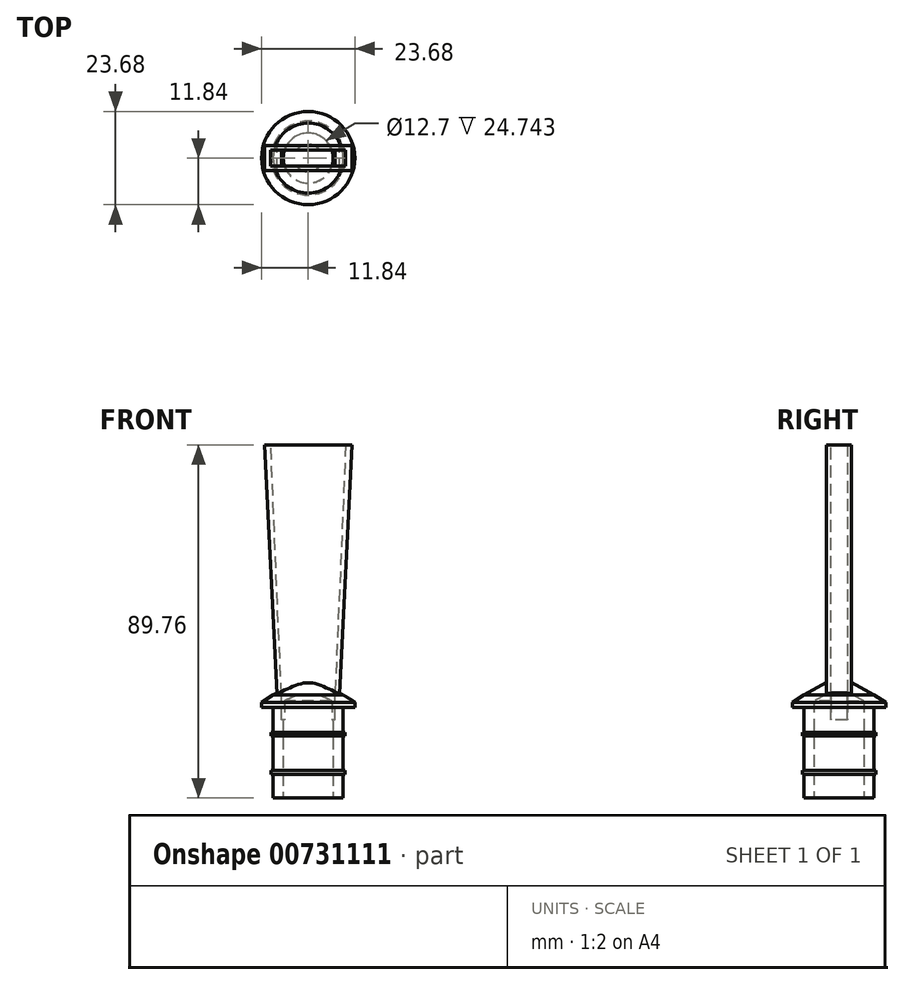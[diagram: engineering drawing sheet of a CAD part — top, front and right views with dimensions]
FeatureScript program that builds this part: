
annotation { "Feature Type Name" : "Feature", "Feature Type Description" : "" }
export const myFeature = defineFeature(function(context is Context, id is Id, definition is map)
    precondition{}
    {
        {
            var Q0;
            Q0=qCreatedBy(makeId("Top.planeOp"),FACE);
            var sketch = newSketch(context, id + "F0", { "sketchPlane" : qUnion([Q0])});
            skCircle(sketch, "E0", {"center": v(0, 0) * mm, "radius": 8.9 * mm});
            skSolve(sketch);
        }
        {
            var Q0;
            Q0=qSketchRegion(id+"F0",true);
            extrude(context, id + "F1", {"entities" : qUnion([Q0]), "depth" : 6.05 * mm, "offsetDistance" : 25.4 * mm});
        }
        {
            var Q0;
            Q0=makeQuery(id+"F1.opExtrude","CAP_FACE",FACE,{"disambiguationData":[OSD([sQuery(id+"F0.wireOp",EDGE,"E0")])],"isStart":false});
            var sketch = newSketch(context, id + "F2", { "sketchPlane" : qUnion([Q0])});
            skCircle(sketch, "E1", {"center": v(0, 0) * mm, "radius": 9.39 * mm});
            skSolve(sketch);
        }
        {
            var Q0;
            Q0=qSketchRegion(id+"F2",true);
            extrude(context, id + "F3", {"entities" : qUnion([Q0]), "operationType" : NewBodyOperationType.ADD, "depth" : 0.94 * mm, "offsetDistance" : 25.4 * mm});
        }
        {
            var Q0;
            Q0=makeQuery(id+"F3.opExtrude","CAP_FACE",FACE,{"disambiguationData":[OSD([sQuery(id+"F2.wireOp",EDGE,"E1")])],"isStart":false});
            var sketch = newSketch(context, id + "F4", { "sketchPlane" : qUnion([Q0])});
            skCircle(sketch, "E2", {"center": v(0, 0) * mm, "radius": 8.9 * mm});
            skSolve(sketch);
        }
        {
            var Q0;
            Q0=makeQuery(id+"F4.imprint","IMPRINT",FACE,{"disambiguationData":[TD([[makeQuery(id+"F4.imprint","IMPRINT",EDGE,{"derivedFrom":sQuery(id+"F4.wireOp",EDGE,"E2")}),1.0]])]});
            extrude(context, id + "F5", {"entities" : qUnion([Q0]), "operationType" : NewBodyOperationType.ADD, "depth" : 8.76 * mm, "offsetDistance" : 25.4 * mm});
        }
        {
            var Q0;
            Q0=makeQuery(id+"F5.opExtrude","CAP_FACE",FACE,{"disambiguationData":[OSD([sQuery(id+"F4.wireOp",EDGE,"E2")])],"isStart":false});
            var sketch = newSketch(context, id + "F6", { "sketchPlane" : qUnion([Q0])});
            skCircle(sketch, "E3", {"center": v(0, 0) * mm, "radius": 9.39 * mm});
            skSolve(sketch);
        }
        {
            var Q0;
            Q0=qSketchRegion(id+"F6",true);
            extrude(context, id + "F7", {"entities" : qUnion([Q0]), "operationType" : NewBodyOperationType.ADD, "depth" : 1 * mm, "offsetDistance" : 25.4 * mm});
        }
        {
            var Q0;
            Q0=makeQuery(id+"F7.opExtrude","CAP_FACE",FACE,{"disambiguationData":[OSD([sQuery(id+"F6.wireOp",EDGE,"E3")])],"isStart":false});
            var sketch = newSketch(context, id + "F8", { "sketchPlane" : qUnion([Q0])});
            skCircle(sketch, "E4", {"center": v(0, 0) * mm, "radius": 8.9 * mm});
            skSolve(sketch);
        }
        {
            var Q0;
            Q0=qSketchRegion(id+"F8",true);
            extrude(context, id + "F9", {"entities" : qUnion([Q0]), "operationType" : NewBodyOperationType.ADD, "depth" : 6.35 * mm, "offsetDistance" : 25.4 * mm});
        }
        {
            var Q0;
            Q0=qCreatedBy(makeId("Right.planeOp"),FACE);
            var sketch = newSketch(context, id + "F10", { "sketchPlane" : qUnion([Q0])});
            skLineSegment(sketch, "E5", {"start": v(0, 23.09) * mm, "end": v(-11.84, 23.09) * mm});
            skLineSegment(sketch, "E6", {"start": v(-11.84, 23.09) * mm, "end": v(-11.84, 24.36) * mm});
            skLineSegment(sketch, "E7", {"start": v(-11.84, 24.36) * mm, "end": v(-8.9, 26.26) * mm});
            skLineSegment(sketch, "E8", {"start": v(-8.9, 26.26) * mm, "end": v(0, 26.26) * mm});
            skLineSegment(sketch, "E9", {"start": v(0, 26.26) * mm, "end": v(0, 23.09) * mm});
            skSolve(sketch);
        }
        {
            var Q0;
            Q0=makeQuery(id+"F10.imprint","IMPRINT",FACE,{"disambiguationData":[TD([[makeQuery(id+"F10.imprint","IMPRINT",EDGE,{"derivedFrom":sQuery(id+"F10.wireOp",EDGE,"E5")}),-1.0]])]});
            var Q1;
            Q1=makeQuery(id+"F9.opExtrude","SWEPT_FACE",FACE,{"disambiguationData":[OSD([sQuery(id+"F8.wireOp",EDGE,"E4")])]});
            revolve(context, id + "F11", {"operationType" : NewBodyOperationType.ADD, "surfaceOperationType" : NewSurfaceOperationType.NEW, "entities" : qUnion([Q0]), "axis" : qUnion([Q1]), "revolveType" : RevolveType.FULL});
        }
        {
            var Q0;
            Q0=makeQuery(id+"F11.opRevolve","SWEPT_FACE",FACE,{"disambiguationData":[OSD([sQuery(id+"F10.wireOp",EDGE,"E8")])]});
            var sketch = newSketch(context, id + "F12", { "sketchPlane" : qUnion([Q0])});
            skCircle(sketch, "E10", {"center": v(0, 0) * mm, "radius": 8.9 * mm});
            skSolve(sketch);
        }
        {
            var Q0;
            Q0=makeQuery(id+"F12.imprint","IMPRINT",FACE,{"disambiguationData":[TD([[makeQuery(id+"F12.imprint","IMPRINT",EDGE,{"derivedFrom":sQuery(id+"F12.wireOp",EDGE,"E10")}),1.0]])]});
            cPlane(context, id + "F13", {"entities" : qUnion([Q0]), "cplaneType" : CPlaneType.OFFSET, "offset" : 0 * mm, "width" : 152.4 * mm, "height" : 152.4 * mm});
        }
        {
            var Q0;
            Q0=qCreatedBy(id+"F13.planeOp",FACE);
            var sketch = newSketch(context, id + "F14", { "sketchPlane" : qUnion([Q0])});
            skLineSegment(sketch, "E11.bottom", {"start": v(-7.94, 3.17) * mm, "end": v(7.94, 3.17) * mm});
            skLineSegment(sketch, "E11.top", {"start": v(-7.94, -3.18) * mm, "end": v(7.94, -3.18) * mm});
            skLineSegment(sketch, "E11.left", {"start": v(-7.94, 3.17) * mm, "end": v(-7.94, -3.18) * mm});
            skLineSegment(sketch, "E11.right", {"start": v(7.94, 3.17) * mm, "end": v(7.94, -3.18) * mm});
            skLineSegment(sketch, "E12", {"start": v(-7.94, 3.18) * mm, "end": v(7.94, -3.18) * mm, "construction": true});
            skPoint(sketch, "E13", {"position": v(0, 0) * mm});
            skSolve(sketch);
        }
        {
            var Q0;
            Q0=qCreatedBy(makeId("Right.planeOp"),FACE);
            var sketch = newSketch(context, id + "F15", { "sketchPlane" : qUnion([Q0])});
            skLineSegment(sketch, "E14", {"start": v(0, 26.26) * mm, "end": v(8.9, 26.26) * mm});
            skLineSegment(sketch, "E15", {"start": v(8.9, 26.26) * mm, "end": v(0, 31.03) * mm});
            skLineSegment(sketch, "E16", {"start": v(0, 31.03) * mm, "end": v(0, 26.26) * mm});
            skLineSegment(sketch, "E17", {"start": v(8.9, 26.26) * mm, "end": v(11.84, 24.36) * mm, "construction": true});
            skSolve(sketch);
        }
        {
            var Q0;
            Q0=makeQuery(id+"F15.imprint","IMPRINT",FACE,{"disambiguationData":[TD([[makeQuery(id+"F15.imprint","IMPRINT",EDGE,{"derivedFrom":sQuery(id+"F15.wireOp",EDGE,"E14")}),1.0]])]});
            var Q1;
            Q1=makeQuery(id+"F5.opExtrude","SWEPT_FACE",FACE,{"disambiguationData":[OSD([sQuery(id+"F4.wireOp",EDGE,"E2")])]});
            revolve(context, id + "F16", {"operationType" : NewBodyOperationType.ADD, "surfaceOperationType" : NewSurfaceOperationType.NEW, "entities" : qUnion([Q0]), "axis" : qUnion([Q1]), "revolveType" : RevolveType.FULL});
        }
        {
            var Q0;
            Q0=qCreatedBy(id+"F13.planeOp",FACE);
            cPlane(context, id + "F17", {"entities" : qUnion([Q0]), "cplaneType" : CPlaneType.OFFSET, "offset" : 63.5 * mm, "width" : 152.4 * mm, "height" : 152.4 * mm});
        }
        {
            var Q0;
            Q0=qCreatedBy(id+"F17.planeOp",FACE);
            var sketch = newSketch(context, id + "F18", { "sketchPlane" : qUnion([Q0])});
            skLineSegment(sketch, "E18.bottom", {"start": v(-5.56, 3.18) * mm, "end": v(5.56, 3.18) * mm});
            skLineSegment(sketch, "E18.top", {"start": v(-5.56, -3.18) * mm, "end": v(5.56, -3.18) * mm});
            skLineSegment(sketch, "E18.left", {"start": v(-5.56, 3.18) * mm, "end": v(-5.56, -3.18) * mm});
            skLineSegment(sketch, "E18.right", {"start": v(5.56, 3.18) * mm, "end": v(5.56, -3.18) * mm});
            skLineSegment(sketch, "E19", {"start": v(-5.56, 3.18) * mm, "end": v(5.56, -3.18) * mm, "construction": true});
            skPoint(sketch, "E20", {"position": v(0, 0) * mm});
            skSolve(sketch);
        }
        {
            var Q1;
            Q1=qSketchRegion(id+"F14",true);
            var Q2;
            Q2=qSketchRegion(id+"F18",true);
            loft(context, id + "F19", {"operationType" : NewBodyOperationType.ADD, "sheetProfilesArray" : [{ "sheetProfileEntities" : qUnion([Q1]) }, { "sheetProfileEntities" : qUnion([Q2]) }]});
        }
        {
            var Q0;
            Q0=makeQuery(id+"F19.opLoft","CAP_FACE",FACE,{"disambiguationData":[OSD([makeQuery(id+"F18.imprint","IMPRINT",FACE,{"disambiguationData":[TD([[makeQuery(id+"F18.imprint","IMPRINT",EDGE,{"derivedFrom":sQuery(id+"F18.wireOp",EDGE,"E18.bottom")}),-1.0]])]})])],"isStart":true});
            var sketch = newSketch(context, id + "F20", { "sketchPlane" : qUnion([Q0])});
            skLineSegment(sketch, "E21.bottom", {"start": v(-4.44, 2.06) * mm, "end": v(4.45, 2.06) * mm});
            skLineSegment(sketch, "E21.top", {"start": v(-4.44, -2.06) * mm, "end": v(4.45, -2.06) * mm});
            skLineSegment(sketch, "E21.left", {"start": v(-4.45, 2.06) * mm, "end": v(-4.45, -2.06) * mm});
            skLineSegment(sketch, "E21.right", {"start": v(4.45, 2.06) * mm, "end": v(4.45, -2.06) * mm});
            skSolve(sketch);
        }
        {
            var Q0;
            Q0=qCreatedBy(id+"F13.planeOp",FACE);
            var sketch = newSketch(context, id + "F21", { "sketchPlane" : qUnion([Q0])});
            skLineSegment(sketch, "E22.bottom", {"start": v(-6.82, 2.06) * mm, "end": v(6.82, 2.06) * mm});
            skLineSegment(sketch, "E22.top", {"start": v(-6.82, -2.06) * mm, "end": v(6.82, -2.06) * mm});
            skLineSegment(sketch, "E22.left", {"start": v(-6.82, 2.06) * mm, "end": v(-6.82, -2.06) * mm});
            skLineSegment(sketch, "E22.right", {"start": v(6.82, 2.06) * mm, "end": v(6.82, -2.06) * mm});
            skFitSpline(sketch, "E23.0", {"points": [v(-7.93, -3.18) * mm, v(-7.92, -2.13) * mm, v(-7.92, -0.8) * mm, v(-7.92, 0.79) * mm, v(-7.92, 1.86) * mm, v(-7.93, 2.65) * mm, v(-7.93, 3.17) * mm], "construction": true});
            skFitSpline(sketch, "E24.0", {"points": [v(7.93, 3.18) * mm, v(7.92, 2.13) * mm, v(7.92, 0.8) * mm, v(7.92, -0.79) * mm, v(7.92, -1.86) * mm, v(7.93, -2.65) * mm, v(7.93, -3.18) * mm], "construction": true});
            skSolve(sketch);
        }
        {
            var Q0;
            Q0=qSketchRegion(id+"F20",true);
            var Q1;
            Q1=qSketchRegion(id+"F21",true);
            loft(context, id + "F22", {"operationType" : NewBodyOperationType.REMOVE, "sheetProfilesArray" : [{ "sheetProfileEntities" : qUnion([Q0]) }, { "sheetProfileEntities" : qUnion([Q1]) }]});
        }
        {
            var Q0;
            Q0=makeQuery(id+"F22.boolean.opBoolean","COPY",FACE,{"derivedFrom":makeQuery(id+"F22.opLoft","CAP_FACE",FACE,{"disambiguationData":[OSD([makeQuery(id+"F21.imprint","IMPRINT",FACE,{"disambiguationData":[TD([[makeQuery(id+"F21.imprint","IMPRINT",EDGE,{"derivedFrom":sQuery(id+"F21.wireOp",EDGE,"E22.bottom")}),-1.0]])]})])],"isStart":true})});
            var Q1;
            Q1=makeQuery(id+"F1.opExtrude","CAP_FACE",FACE,{"disambiguationData":[OSD([sQuery(id+"F0.wireOp",EDGE,"E0")])],"isStart":true});
            shell(context, id + "F23", {"entities" : qUnion([Q0, Q1]), "thickness" : 2.54 * mm});
        }
        {
            var Q0;
            Q0=qCreatedBy(id+"F13.planeOp",FACE);
            var sketch = newSketch(context, id + "F24", { "sketchPlane" : qUnion([Q0])});
            skLineSegment(sketch, "E25.0", {"start": v(2.84, -2.06) * mm, "end": v(-2.84, -2.06) * mm});
            skLineSegment(sketch, "E26.0", {"start": v(6.82, -2.06) * mm, "end": v(2.84, -2.06) * mm});
            skLineSegment(sketch, "E27.0", {"start": v(6.82, 2.06) * mm, "end": v(6.82, -2.06) * mm});
            skLineSegment(sketch, "E28.0", {"start": v(2.84, 2.06) * mm, "end": v(6.82, 2.06) * mm});
            skLineSegment(sketch, "E29.0", {"start": v(-2.84, 2.06) * mm, "end": v(2.84, 2.06) * mm});
            skLineSegment(sketch, "E30.0", {"start": v(-6.82, 2.06) * mm, "end": v(-2.84, 2.06) * mm});
            skLineSegment(sketch, "E31.0", {"start": v(-2.84, -2.06) * mm, "end": v(-6.82, -2.06) * mm});
            skLineSegment(sketch, "E32.0", {"start": v(-6.82, -2.06) * mm, "end": v(-6.82, 2.06) * mm});
            skSolve(sketch);
        }
        {
            var Q0;
            Q0=makeQuery(id+"F19.opLoft","SWEPT_FACE",FACE,{"disambiguationData":[OSD([sQuery(id+"F14.wireOp",EDGE,"E11.bottom"),sQuery(id+"F14.wireOp",EDGE,"E11.left"),sQuery(id+"F14.wireOp",EDGE,"E11.right"),sQuery(id+"F18.wireOp",EDGE,"E18.bottom"),sQuery(id+"F18.wireOp",EDGE,"E18.left"),sQuery(id+"F18.wireOp",EDGE,"E18.right")])]});
            var sketch = newSketch(context, id + "F25", { "sketchPlane" : qUnion([Q0])});
            skLineSegment(sketch, "E33.0", {"start": v(5.56, 89.76) * mm, "end": v(-5.56, 89.76) * mm});
            skLineSegment(sketch, "E34.0", {"start": v(-5.8, 83.42) * mm, "end": v(-5.56, 89.76) * mm});
            skLineSegment(sketch, "E35", {"start": v(-5.8, 83.42) * mm, "end": v(5.56, 89.76) * mm});
            skPoint(sketch, "E36.orphan", {"position": v(-7.93, 26.45) * mm});
            skSolve(sketch);
        }
        {
            var Q0;
            Q0=makeQuery(id+"F19.opLoft","SWEPT_FACE",FACE,{"disambiguationData":[OSD([sQuery(id+"F14.wireOp",EDGE,"E11.top"),sQuery(id+"F14.wireOp",EDGE,"E11.left"),sQuery(id+"F14.wireOp",EDGE,"E11.right"),sQuery(id+"F18.wireOp",EDGE,"E18.top"),sQuery(id+"F18.wireOp",EDGE,"E18.left"),sQuery(id+"F18.wireOp",EDGE,"E18.right")])]});
            var sketch = newSketch(context, id + "F26", { "sketchPlane" : qUnion([Q0])});
            skLineSegment(sketch, "E37", {"start": v(7.93, 26.45) * mm, "end": v(5.56, 89.76) * mm});
            skLineSegment(sketch, "E38", {"start": v(5.56, 89.76) * mm, "end": v(11.11, 89.76) * mm});
            skLineSegment(sketch, "E39", {"start": v(11.11, 89.76) * mm, "end": v(7.93, 26.45) * mm});
            skLineSegment(sketch, "E40", {"start": v(-7.93, 26.45) * mm, "end": v(-5.56, 89.76) * mm});
            skLineSegment(sketch, "E41", {"start": v(-5.56, 89.76) * mm, "end": v(-11.11, 89.76) * mm});
            skLineSegment(sketch, "E42", {"start": v(-11.11, 89.76) * mm, "end": v(-7.93, 26.45) * mm});
            skSolve(sketch);
        }
        {
            var Q0;
            Q0 = qSketchRegion(id + "F26", true);
            var Q1;
            Q1=makeQuery(id+"F19.opLoft","SWEPT_FACE",FACE,{"disambiguationData":[OSD([sQuery(id+"F14.wireOp",EDGE,"E11.bottom"),sQuery(id+"F14.wireOp",EDGE,"E11.left"),sQuery(id+"F14.wireOp",EDGE,"E11.right"),sQuery(id+"F18.wireOp",EDGE,"E18.bottom"),sQuery(id+"F18.wireOp",EDGE,"E18.left"),sQuery(id+"F18.wireOp",EDGE,"E18.right")])]});
            extrude(context, id + "F27", {"entities" : qUnion([Q0]), "operationType" : NewBodyOperationType.ADD, "endBound" : BoundingType.UP_TO_SURFACE, "oppositeDirection" : true, "depth" : 25.4 * mm, "endBoundEntityFace" : qUnion([Q1]), "offsetDistance" : 25.4 * mm});
        }
        {
            var Q0;
            Q0=qCreatedBy(makeId("Front.planeOp"),FACE);
            var sketch = newSketch(context, id + "F28", { "sketchPlane" : qUnion([Q0])});
            skLineSegment(sketch, "E43", {"start": v(-6.82, 26.26) * mm, "end": v(-9.52, 89.76) * mm});
            skLineSegment(sketch, "E44", {"start": v(-9.52, 89.76) * mm, "end": v(9.52, 89.76) * mm});
            skLineSegment(sketch, "E45", {"start": v(9.53, 89.76) * mm, "end": v(6.82, 26.26) * mm});
            skLineSegment(sketch, "E46", {"start": v(6.82, 26.26) * mm, "end": v(-6.82, 26.26) * mm});
            skSolve(sketch);
        }
        {
            var Q0;
            Q0 = qSketchRegion(id + "F28", true);
            var Q1;
            Q1=makeQuery(id+"F22.boolean.opBoolean","COPY",FACE,{"derivedFrom":makeQuery(id+"F22.opLoft","SWEPT_FACE",FACE,{"disambiguationData":[OSD([sQuery(id+"F20.wireOp",EDGE,"E21.bottom"),sQuery(id+"F20.wireOp",EDGE,"E21.left"),sQuery(id+"F20.wireOp",EDGE,"E21.right"),sQuery(id+"F21.wireOp",EDGE,"E22.bottom"),sQuery(id+"F21.wireOp",EDGE,"E22.left"),sQuery(id+"F21.wireOp",EDGE,"E22.right")])]})});
            var Q2;
            Q2=makeQuery(id+"F22.boolean.opBoolean","COPY",FACE,{"derivedFrom":makeQuery(id+"F22.opLoft","SWEPT_FACE",FACE,{"disambiguationData":[OSD([sQuery(id+"F20.wireOp",EDGE,"E21.top"),sQuery(id+"F20.wireOp",EDGE,"E21.left"),sQuery(id+"F20.wireOp",EDGE,"E21.right"),sQuery(id+"F21.wireOp",EDGE,"E22.top"),sQuery(id+"F21.wireOp",EDGE,"E22.left"),sQuery(id+"F21.wireOp",EDGE,"E22.right")])]})});
            extrude(context, id + "F29", {"entities" : qUnion([Q0]), "operationType" : NewBodyOperationType.REMOVE, "endBound" : BoundingType.UP_TO_SURFACE, "oppositeDirection" : true, "depth" : 25.4 * mm, "endBoundEntityFace" : qUnion([Q1]), "offsetDistance" : 25.4 * mm, "hasSecondDirection" : true, "secondDirectionBound" : SecondDirectionBoundingType.UP_TO_SURFACE, "secondDirectionOppositeDirection" : false, "secondDirectionDepth" : 25.4 * mm, "secondDirectionBoundEntityFace" : qUnion([Q2])});
        }
        {
            var Q0;
            Q0=qCreatedBy(makeId("Right.planeOp"),FACE);
            var sketch = newSketch(context, id + "F30", { "sketchPlane" : qUnion([Q0])});
            skLineSegment(sketch, "E47", {"start": v(3.21, 89.76) * mm, "end": v(-3.17, 78.7) * mm});
            skLineSegment(sketch, "E48", {"start": v(-3.18, 78.7) * mm, "end": v(-3.18, 89.76) * mm});
            skLineSegment(sketch, "E49", {"start": v(-3.18, 89.76) * mm, "end": v(3.21, 89.76) * mm});
            skSolve(sketch);
        }
        {
            var Q0;
            Q0=makeQuery(id+"F24.imprint","IMPRINT",FACE,{"disambiguationData":[TD([[makeQuery(id+"F24.imprint","IMPRINT",EDGE,{"derivedFrom":sQuery(id+"F24.wireOp",EDGE,"E25.0")}),-1.0]])]});
            var sketch = newSketch(context, id + "F31", { "sketchPlane" : qUnion([Q0])});
            skLineSegment(sketch, "E50.0", {"start": v(-6.82, -2.06) * mm, "end": v(-6.82, 2.06) * mm});
            skLineSegment(sketch, "E51.0", {"start": v(-6.82, 2.06) * mm, "end": v(-2.84, 2.06) * mm});
            skLineSegment(sketch, "E52.0", {"start": v(-2.84, 2.06) * mm, "end": v(2.84, 2.06) * mm});
            skLineSegment(sketch, "E53.0", {"start": v(2.84, 2.06) * mm, "end": v(6.82, 2.06) * mm});
            skLineSegment(sketch, "E54.0", {"start": v(6.82, 2.06) * mm, "end": v(6.82, -2.06) * mm});
            skLineSegment(sketch, "E55.0", {"start": v(6.82, -2.06) * mm, "end": v(2.84, -2.06) * mm});
            skLineSegment(sketch, "E56.0", {"start": v(2.84, -2.06) * mm, "end": v(-2.84, -2.06) * mm});
            skLineSegment(sketch, "E57.0", {"start": v(-2.84, -2.06) * mm, "end": v(-6.82, -2.06) * mm});
            skSolve(sketch);
        }
        {
            var Q0;
            Q0 = qSketchRegion(id + "F31", true);
            extrude(context, id + "F32", {"entities" : qUnion([Q0]), "operationType" : NewBodyOperationType.REMOVE, "oppositeDirection" : true, "depth" : 6.35 * mm, "offsetDistance" : 25.4 * mm});
        }
    });
